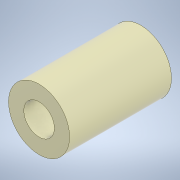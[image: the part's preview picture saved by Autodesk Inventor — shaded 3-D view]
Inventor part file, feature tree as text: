
AUTODESK INVENTOR PART (.ipt)
format: ipt  version: 2020.2 (Build 242310000, 310)  size: 101,376 bytes
history: native  units: mm
features: other x1, extrude x1, sketch x1
ambient origin geometry x8: Origin, YZ Plane, XZ Plane, XY Plane, X Axis, Y Axis, Z Axis, Center Point
bodies: Body1 (feature_tree)
feature tree (3):
  other  "ソリッド1"
  extrude  "押し出し1"  Depth=6.0mm
  sketch  "スケッチ1"
